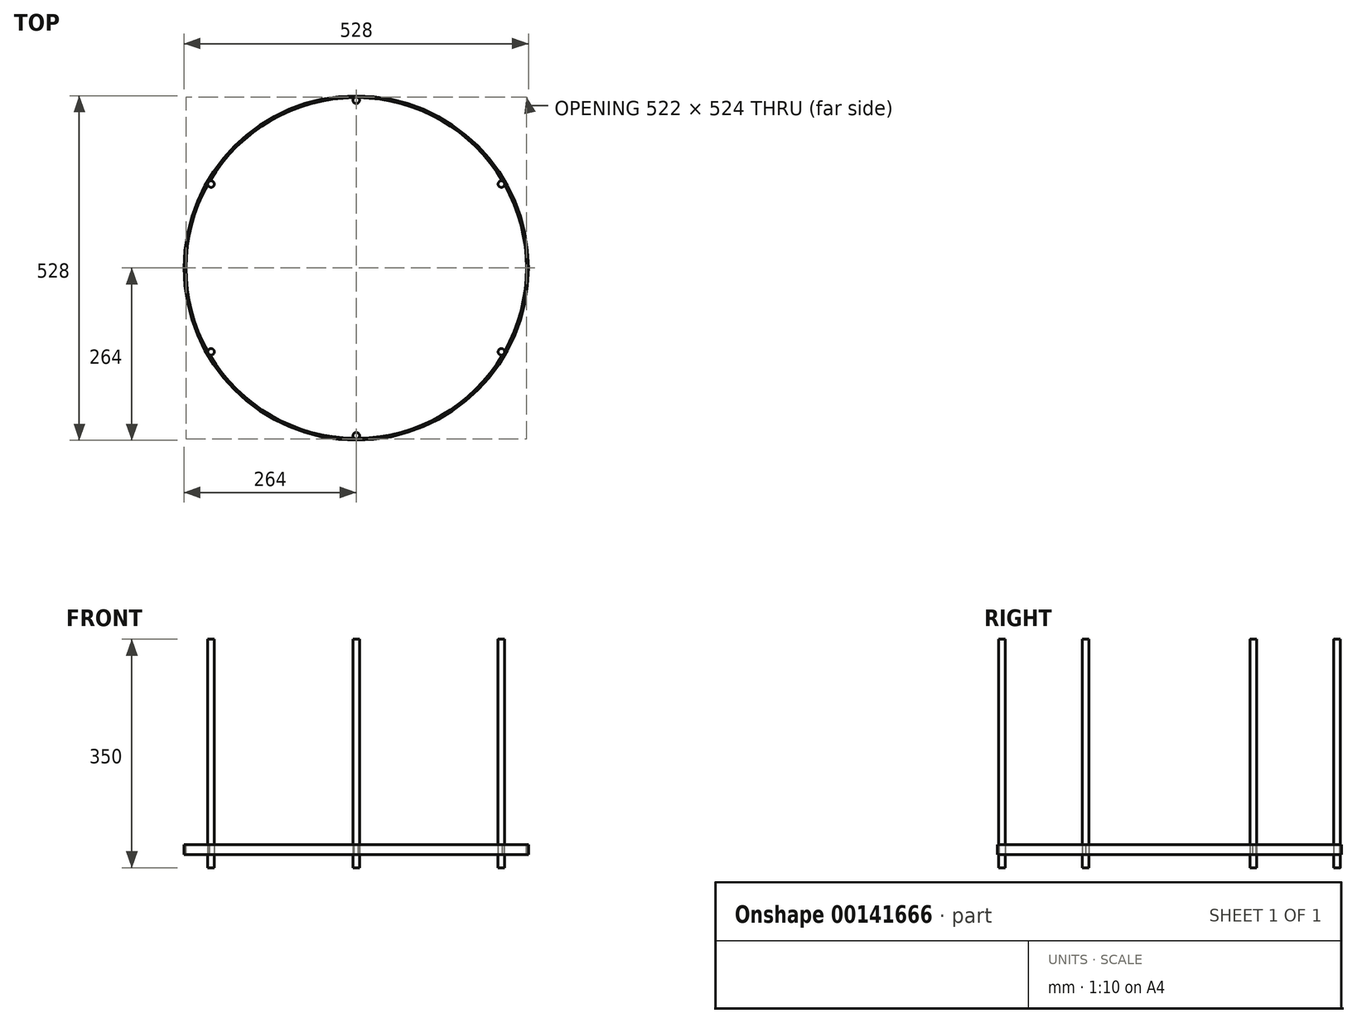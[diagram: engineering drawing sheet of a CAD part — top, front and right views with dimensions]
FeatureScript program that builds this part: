
annotation { "Feature Type Name" : "Feature", "Feature Type Description" : "" }
export const myFeature = defineFeature(function(context is Context, id is Id, definition is map)
    precondition{}
    {
        {
            var Q0;
            Q0=qCreatedBy(makeId("Top.planeOp"),FACE);
            var sketch = newSketch(context, id + "F0", { "sketchPlane" : qUnion([Q0])});
            skCircle(sketch, "E0", {"center": v(0, 0) * mm, "radius": 252 * mm});
            skCircle(sketch, "E1", {"center": v(0, 257) * mm, "radius": 5 * mm});
            skSolve(sketch);
        }
        {
            var Q0;
            Q0=makeQuery(id+"F0.imprint","IMPRINT",FACE,{"disambiguationData":[TD([[makeQuery(id+"F0.imprint","IMPRINT",EDGE,{"derivedFrom":sQuery(id+"F0.wireOp",EDGE,"E1")}),1.0]])]});
            extrude(context, id + "F1", {"entities" : qUnion([Q0]), "depth" : 350 * mm});
        }
        {
            var Q0;
            Q0=qCreatedBy(makeId("Right.planeOp"),FACE);
            var sketch = newSketch(context, id + "F2", { "sketchPlane" : qUnion([Q0])});
            skLineSegment(sketch, "E2.bottom", {"start": v(261, 0) * mm, "end": v(264, 0) * mm});
            skLineSegment(sketch, "E2.top", {"start": v(261, 15) * mm, "end": v(264, 15) * mm});
            skLineSegment(sketch, "E2.left", {"start": v(261, 0) * mm, "end": v(261, 15) * mm});
            skLineSegment(sketch, "E2.right", {"start": v(264, 0) * mm, "end": v(264, 15) * mm});
            skSolve(sketch);
        }
        {
            var Q0;
            Q0=qCreatedBy(makeId("Right.planeOp"),FACE);
            var sketch = newSketch(context, id + "F3", { "sketchPlane" : qUnion([Q0])});
            skLineSegment(sketch, "E3", {"start": v(0, 0) * mm, "end": v(0, -89.8) * mm});
            skSolve(sketch);
        }
        {
            var Q0;
            Q0=qCreatedBy(makeId("Front.planeOp"),FACE);
            var sketch = newSketch(context, id + "F4", { "sketchPlane" : qUnion([Q0])});
            skLineSegment(sketch, "E4", {"start": v(0, 0) * mm, "end": v(0, -115.44) * mm});
            skSolve(sketch);
        }
        {
            var Q0;
            Q0=makeQuery(id+"F1.opExtrude","SWEPT_BODY",BODY,{"disambiguationData":[OSD([sQuery(id+"F0.wireOp",EDGE,"E1")])]});
            transform(context, id + "F5", {"entities" : qUnion([Q0]), "transformType" : TransformType.TRANSLATION_3D, "dx" : 0 * mm, "dy" : 0 * mm, "dz" : -20 * mm, "makeCopy" : false});
        }
        {
            var Q0;
            Q0=makeQuery(id+"F2.imprint","IMPRINT",FACE,{"disambiguationData":[TD([[makeQuery(id+"F2.imprint","IMPRINT",EDGE,{"derivedFrom":sQuery(id+"F2.wireOp",EDGE,"E2.bottom")}),1.0]])]});
            var Q1;
            Q1=sQuery(id+"F4.wireOp",EDGE,"E4");
            revolve(context, id + "F6", {"operationType" : NewBodyOperationType.ADD, "entities" : qUnion([Q0]), "axis" : qUnion([Q1]), "revolveType" : RevolveType.FULL});
        }
        {
            var Q0;
            Q0=makeQuery(id+"F1.opExtrude","SWEPT_BODY",BODY,{"disambiguationData":[OSD([sQuery(id+"F0.wireOp",EDGE,"E1")])]});
            var Q1;
            Q1=sQuery(id+"F3.wireOp",EDGE,"E3");
            circularPattern(context, id + "F7", {"operationType" : NewBodyOperationType.ADD, "entities" : qUnion([Q0]), "axis" : qUnion([Q1]), "angle" : 60 * degree, "instanceCount" : 6});
        }
    });
